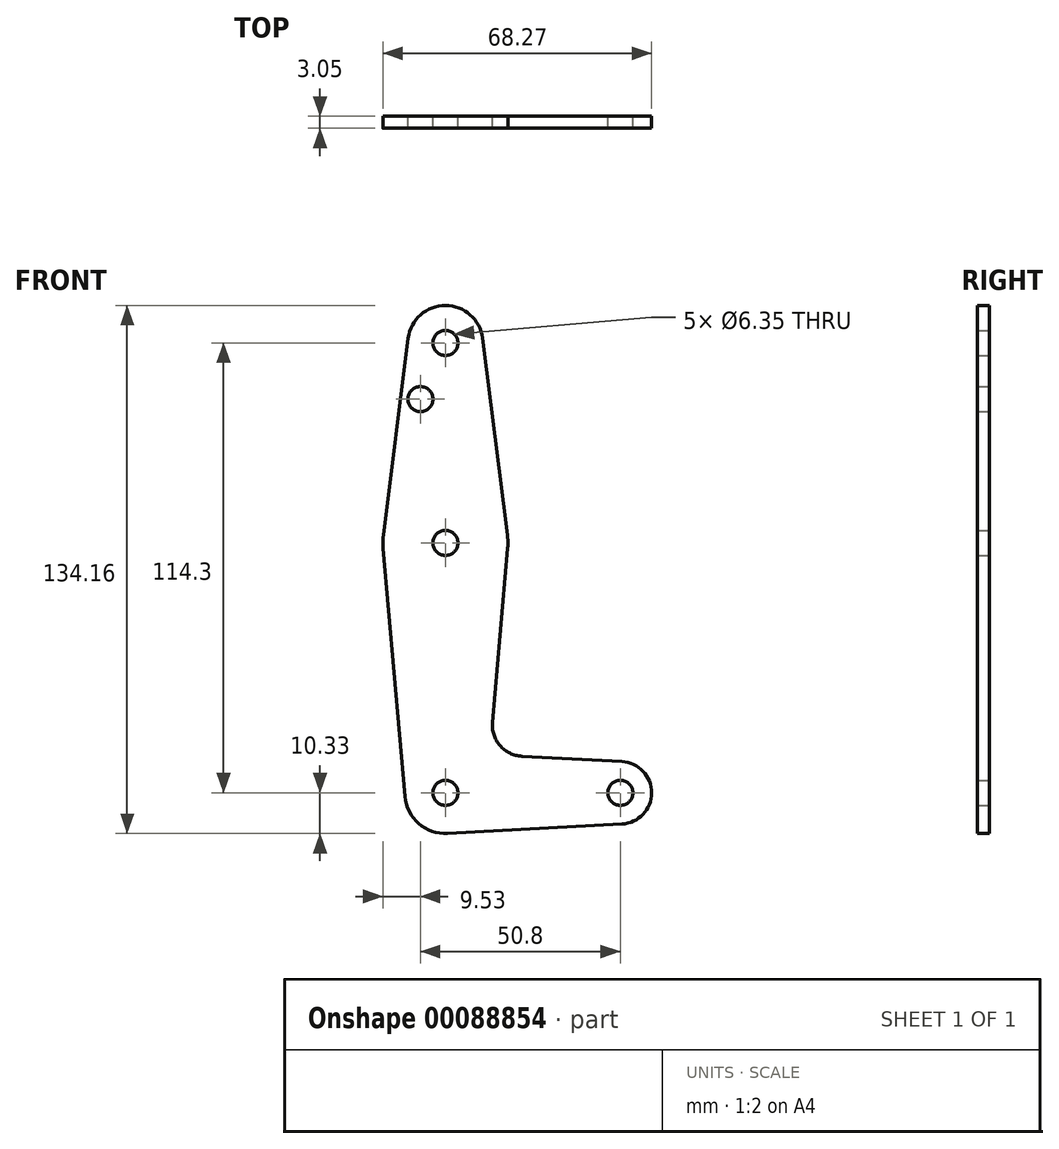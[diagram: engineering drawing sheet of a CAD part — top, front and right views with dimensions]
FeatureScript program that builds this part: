
annotation { "Feature Type Name" : "Feature", "Feature Type Description" : "" }
export const myFeature = defineFeature(function(context is Context, id is Id, definition is map)
    precondition{}
    {
        {
            var Q0;
            Q0=qCreatedBy(makeId("Front.planeOp"),FACE);
            var sketch = newSketch(context, id + "F0", { "sketchPlane" : qUnion([Q0])});
            skLineSegment(sketch, "E0", {"start": v(0, 0) * mm, "end": v(44.45, 0) * mm, "construction": true});
            skCircle(sketch, "E1", {"center": v(0, 114.3) * mm, "radius": 9.53 * mm});
            skCircle(sketch, "E2", {"center": v(0, 63.5) * mm, "radius": 15.88 * mm});
            skCircle(sketch, "E3", {"center": v(44.45, 0) * mm, "radius": 7.94 * mm});
            skCircle(sketch, "E4", {"center": v(0, 0) * mm, "radius": 10.33 * mm});
            skLineSegment(sketch, "E5", {"start": v(0, 114.3) * mm, "end": v(0, 0) * mm, "construction": true});
            skLineSegment(sketch, "E6", {"start": v(-9.45, 115.5) * mm, "end": v(-15.75, 65.48) * mm});
            skLineSegment(sketch, "E7", {"start": v(9.45, 115.5) * mm, "end": v(15.75, 65.48) * mm});
            skCircle(sketch, "E8", {"center": v(0, 114.3) * mm, "radius": 3.18 * mm});
            skCircle(sketch, "E9", {"center": v(0, 0) * mm, "radius": 3.18 * mm});
            skCircle(sketch, "E10", {"center": v(44.45, 0) * mm, "radius": 3.18 * mm});
            skLineSegment(sketch, "E11", {"start": v(0.55, -10.31) * mm, "end": v(44.88, -7.93) * mm});
            skLineSegment(sketch, "E12", {"start": v(15.81, 62.11) * mm, "end": v(11.94, 17.93) * mm});
            skLineSegment(sketch, "E13", {"start": v(19.43, 9.3) * mm, "end": v(44.88, 7.93) * mm});
            skArc(sketch, "E14.filletArc", {"start": v(11.94, 17.93) * mm, "mid": v(13.85, 12.02) * mm, "end": v(19.43, 9.3) * mm});
            skCircle(sketch, "E15", {"center": v(0, 63.5) * mm, "radius": 3.18 * mm});
            skLineSegment(sketch, "E16", {"start": v(-15.81, 62.11) * mm, "end": v(-10.29, -0.9) * mm});
            skCircle(sketch, "E17", {"center": v(-6.35, 100.03) * mm, "radius": 3.18 * mm});
            skSolve(sketch);
        }
        {
            var Q0;
            Q0 = qSketchRegion(id + "F0", true);
            extrude(context, id + "F1", {"entities" : qUnion([Q0]), "depth" : 3.05 * mm});
        }
    });
